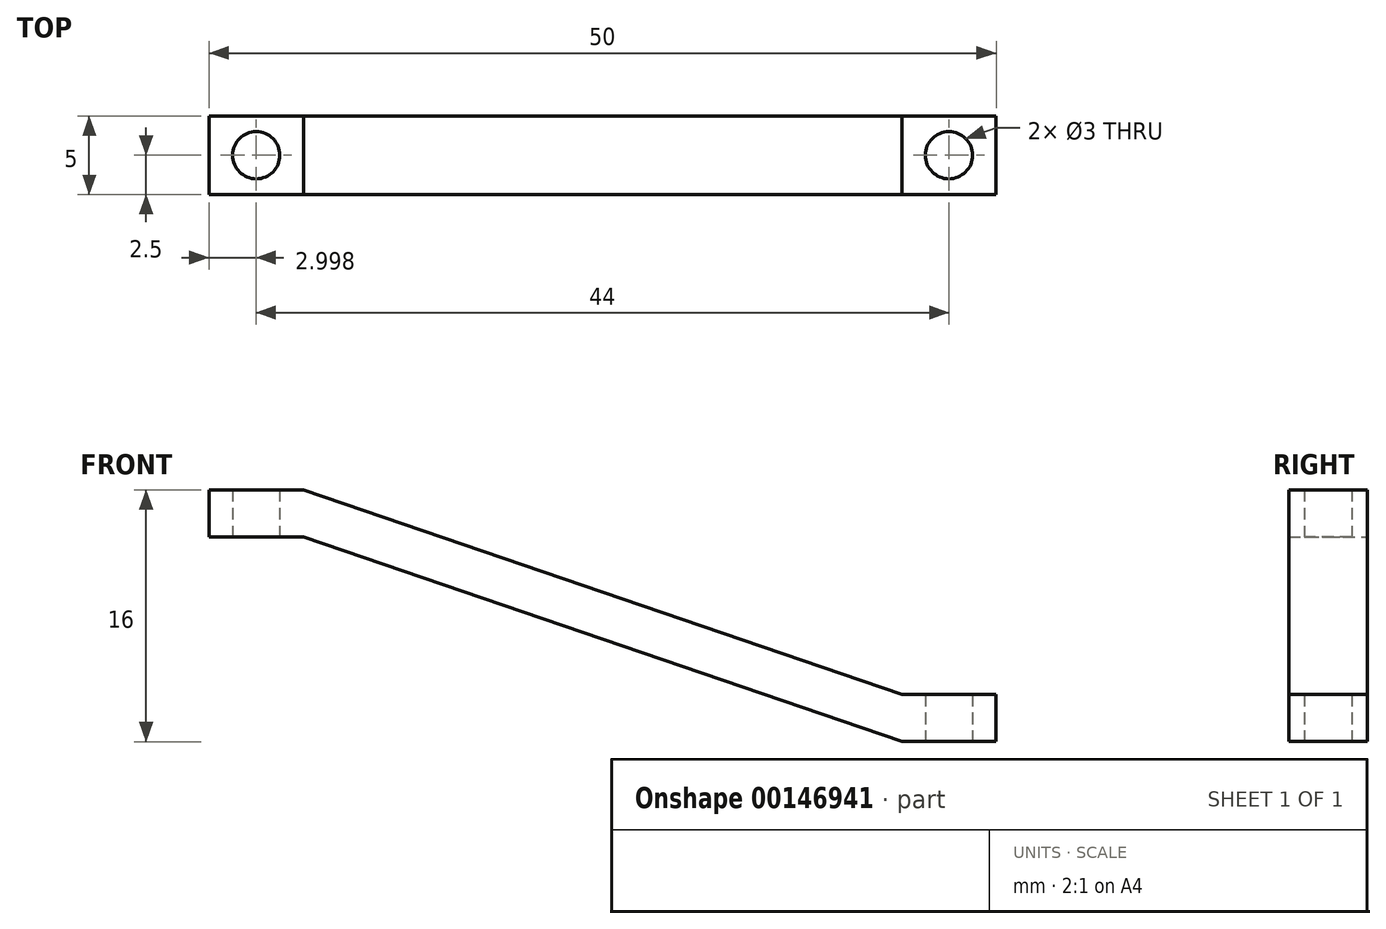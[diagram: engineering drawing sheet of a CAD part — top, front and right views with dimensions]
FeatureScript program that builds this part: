
annotation { "Feature Type Name" : "Feature", "Feature Type Description" : "" }
export const myFeature = defineFeature(function(context is Context, id is Id, definition is map)
    precondition{}
    {
        {
            var Q0;
            Q0=qCreatedBy(makeId("Front.planeOp"),FACE);
            var sketch = newSketch(context, id + "F0", { "sketchPlane" : qUnion([Q0])});
            skLineSegment(sketch, "E0.bottom", {"start": v(-15.82, 43.94) * mm, "end": v(-9.82, 43.94) * mm});
            skLineSegment(sketch, "E0.top", {"start": v(-15.82, 40.94) * mm, "end": v(-9.82, 40.94) * mm});
            skLineSegment(sketch, "E0.left", {"start": v(-15.82, 43.94) * mm, "end": v(-15.82, 40.94) * mm});
            skLineSegment(sketch, "E0.right", {"start": v(-9.82, 43.94) * mm, "end": v(-9.82, 40.94) * mm});
            skLineSegment(sketch, "E1.bottom", {"start": v(28.18, 30.94) * mm, "end": v(34.18, 30.94) * mm});
            skLineSegment(sketch, "E1.top", {"start": v(28.18, 27.94) * mm, "end": v(34.18, 27.94) * mm});
            skLineSegment(sketch, "E1.left", {"start": v(28.18, 30.94) * mm, "end": v(28.18, 27.94) * mm});
            skLineSegment(sketch, "E1.right", {"start": v(34.18, 30.94) * mm, "end": v(34.18, 27.94) * mm});
            skLineSegment(sketch, "E2", {"start": v(-9.82, 43.94) * mm, "end": v(28.18, 30.94) * mm});
            skLineSegment(sketch, "E3", {"start": v(28.18, 27.94) * mm, "end": v(-9.82, 40.94) * mm});
            skSolve(sketch);
        }
        {
            var Q0;
            Q0 = qSketchRegion(id + "F0", true);
            extrude(context, id + "F1", {"entities" : qUnion([Q0]), "depth" : 5 * mm});
        }
        {
            var Q0;
            Q0=qCreatedBy(makeId("Top.planeOp"),FACE);
            var sketch = newSketch(context, id + "F2", { "sketchPlane" : qUnion([Q0])});
            skLineSegment(sketch, "E4", {"start": v(-15.82, -2.5) * mm, "end": v(-9.82, -2.5) * mm, "construction": true});
            skLineSegment(sketch, "E5", {"start": v(-12.82, 0) * mm, "end": v(-12.82, -5) * mm, "construction": true});
            skCircle(sketch, "E6", {"center": v(-12.82, -2.5) * mm, "radius": 1.5 * mm});
            skLineSegment(sketch, "E7", {"start": v(28.18, -2.5) * mm, "end": v(34.18, -2.5) * mm, "construction": true});
            skLineSegment(sketch, "E8", {"start": v(31.18, 0) * mm, "end": v(31.18, -5) * mm, "construction": true});
            skCircle(sketch, "E9", {"center": v(31.18, -2.5) * mm, "radius": 1.5 * mm});
            skSolve(sketch);
        }
        {
            var Q0;
            Q0=makeQuery(id+"F2.imprint","IMPRINT",FACE,{"disambiguationData":[TD([[makeQuery(id+"F2.imprint","IMPRINT",EDGE,{"derivedFrom":sQuery(id+"F2.wireOp",EDGE,"E6")}),1.0]])]});
            var Q1;
            Q1=sQuery(id+"F2.wireOp",EDGE,"E6");
            extrude(context, id + "F3", {"entities" : qUnion([Q0]), "operationType" : NewBodyOperationType.REMOVE, "surfaceEntities" : qUnion([Q1]), "depth" : 100 * mm});
        }
        {
            var Q0;
            Q0 = qSketchRegion(id + "F2", true);
            extrude(context, id + "F4", {"entities" : qUnion([Q0]), "operationType" : NewBodyOperationType.REMOVE, "depth" : 100 * mm});
        }
    });
